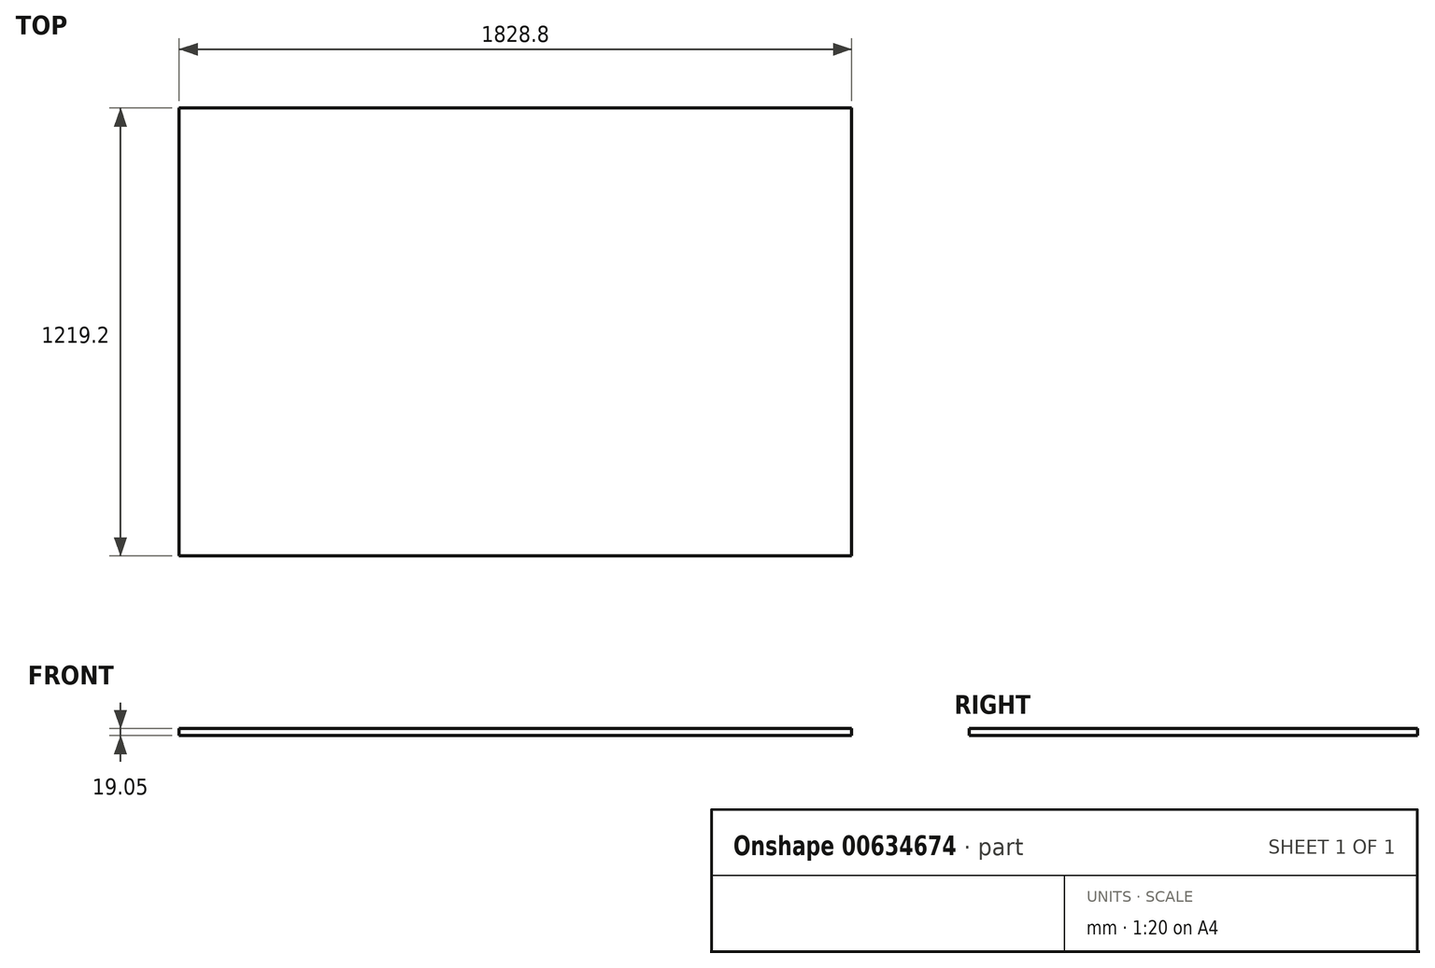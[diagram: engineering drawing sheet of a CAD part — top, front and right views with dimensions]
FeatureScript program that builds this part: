
annotation { "Feature Type Name" : "Feature", "Feature Type Description" : "" }
export const myFeature = defineFeature(function(context is Context, id is Id, definition is map)
    precondition{}
    {
        {
            var Q0;
            Q0=qCreatedBy(makeId("Top.planeOp"),FACE);
            var sketch = newSketch(context, id + "F0", { "sketchPlane" : qUnion([Q0])});
            skLineSegment(sketch, "E0.bottom", {"start": v(-914.4, 609.6) * mm, "end": v(914.4, 609.6) * mm});
            skLineSegment(sketch, "E0.top", {"start": v(-914.4, -609.6) * mm, "end": v(914.4, -609.6) * mm});
            skLineSegment(sketch, "E0.left", {"start": v(-914.4, 609.6) * mm, "end": v(-914.4, -609.6) * mm});
            skLineSegment(sketch, "E0.right", {"start": v(914.4, 609.6) * mm, "end": v(914.4, -609.6) * mm});
            skSolve(sketch);
        }
        {
            var Q0;
            Q0=makeQuery(id+"F0.imprint","IMPRINT",FACE,{"disambiguationData":[TD([[makeQuery(id+"F0.imprint","IMPRINT",EDGE,{"derivedFrom":sQuery(id+"F0.wireOp",EDGE,"E0.bottom")}),-1.0]])]});
            extrude(context, id + "F1", {"entities" : qUnion([Q0]), "depth" : 19.05 * mm});
        }
    });
